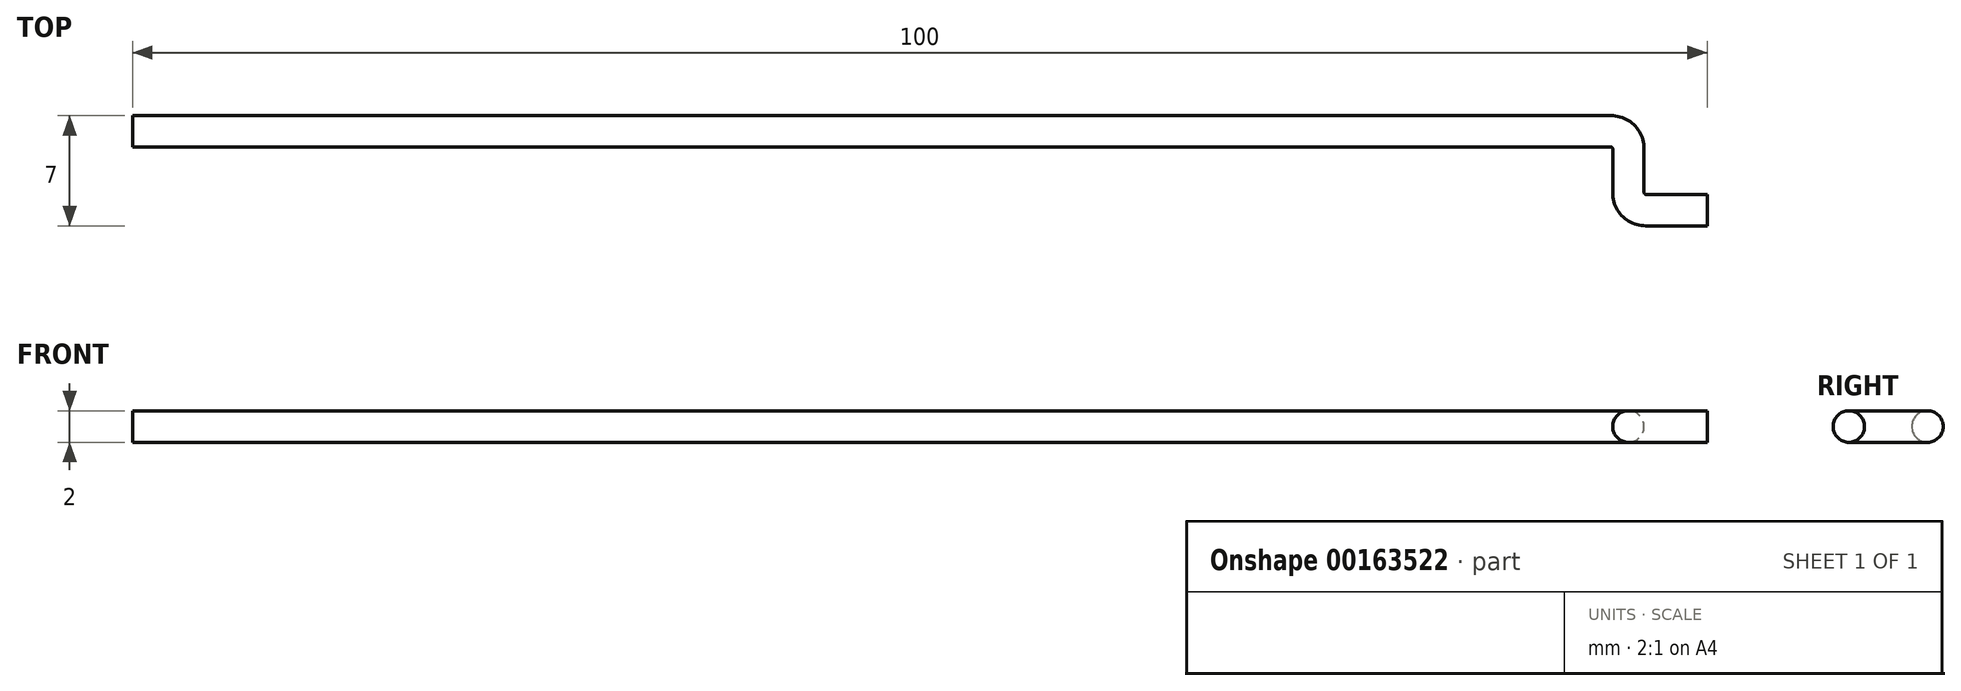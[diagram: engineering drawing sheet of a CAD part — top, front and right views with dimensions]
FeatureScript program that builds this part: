
annotation { "Feature Type Name" : "Feature", "Feature Type Description" : "" }
export const myFeature = defineFeature(function(context is Context, id is Id, definition is map)
    precondition{}
    {
        {
            var Q0;
            Q0=qCreatedBy(makeId("Top.planeOp"),FACE);
            var sketch = newSketch(context, id + "F0", { "sketchPlane" : qUnion([Q0])});
            skLineSegment(sketch, "E0", {"start": v(0, 0) * mm, "end": v(93.9, 0) * mm});
            skLineSegment(sketch, "E1", {"start": v(95, -1.1) * mm, "end": v(95, -3.9) * mm});
            skLineSegment(sketch, "E2", {"start": v(96.1, -5) * mm, "end": v(100, -5) * mm});
            skPoint(sketch, "E3.visualSharp", {"position": v(95, 0) * mm});
            skArc(sketch, "E3.filletArc", {"start": v(95, -1.1) * mm, "mid": v(94.68, -0.32) * mm, "end": v(93.9, 0) * mm});
            skPoint(sketch, "E4.visualSharp", {"position": v(95, -5) * mm});
            skArc(sketch, "E4.filletArc", {"start": v(95, -3.9) * mm, "mid": v(95.32, -4.68) * mm, "end": v(96.1, -5) * mm});
            skSolve(sketch);
        }
        {
            var Q0;
            Q0=qCreatedBy(makeId("Right.planeOp"),FACE);
            var sketch = newSketch(context, id + "F1", { "sketchPlane" : qUnion([Q0])});
            skCircle(sketch, "E5", {"center": v(0, 0) * mm, "radius": 1 * mm});
            skSolve(sketch);
        }
        {
            var Q0;
            Q0=makeQuery(id+"F1.imprint","IMPRINT",FACE,{"disambiguationData":[TD([[makeQuery(id+"F1.imprint","IMPRINT",EDGE,{"derivedFrom":sQuery(id+"F1.wireOp",EDGE,"E5")}),1.0]])]});
            var Q1;
            Q1=sQuery(id+"F0.wireOp",EDGE,"E0");
            var Q2;
            Q2=sQuery(id+"F0.wireOp",EDGE,"E3.filletArc");
            var Q3;
            Q3=sQuery(id+"F0.wireOp",EDGE,"E1");
            var Q4;
            Q4=sQuery(id+"F0.wireOp",EDGE,"E4.filletArc");
            var Q5;
            Q5=sQuery(id+"F0.wireOp",EDGE,"E2");
            sweep(context, id + "F2", {"profiles" : qUnion([Q0]), "path" : qUnion([Q1, Q2, Q3, Q4, Q5])});
        }
        {
            var Q0;
            Q0=makeQuery(id+"F2.opSweep","CAP_FACE",FACE,{"disambiguationData":[OSD([sQuery(id+"F0.wireOp",VERTEX,"E0.start"),sQuery(id+"F1.wireOp",EDGE,"E5")])],"isStart":true});
            var sketch = newSketch(context, id + "F3", { "sketchPlane" : qUnion([Q0])});
            skLineSegment(sketch, "E6", {"start": v(0, 0) * mm, "end": v(1, 0) * mm, "construction": true});
            skLineSegment(sketch, "E7", {"start": v(1, 0) * mm, "end": v(-1, 0) * mm, "construction": true});
            skSolve(sketch);
        }
    });
